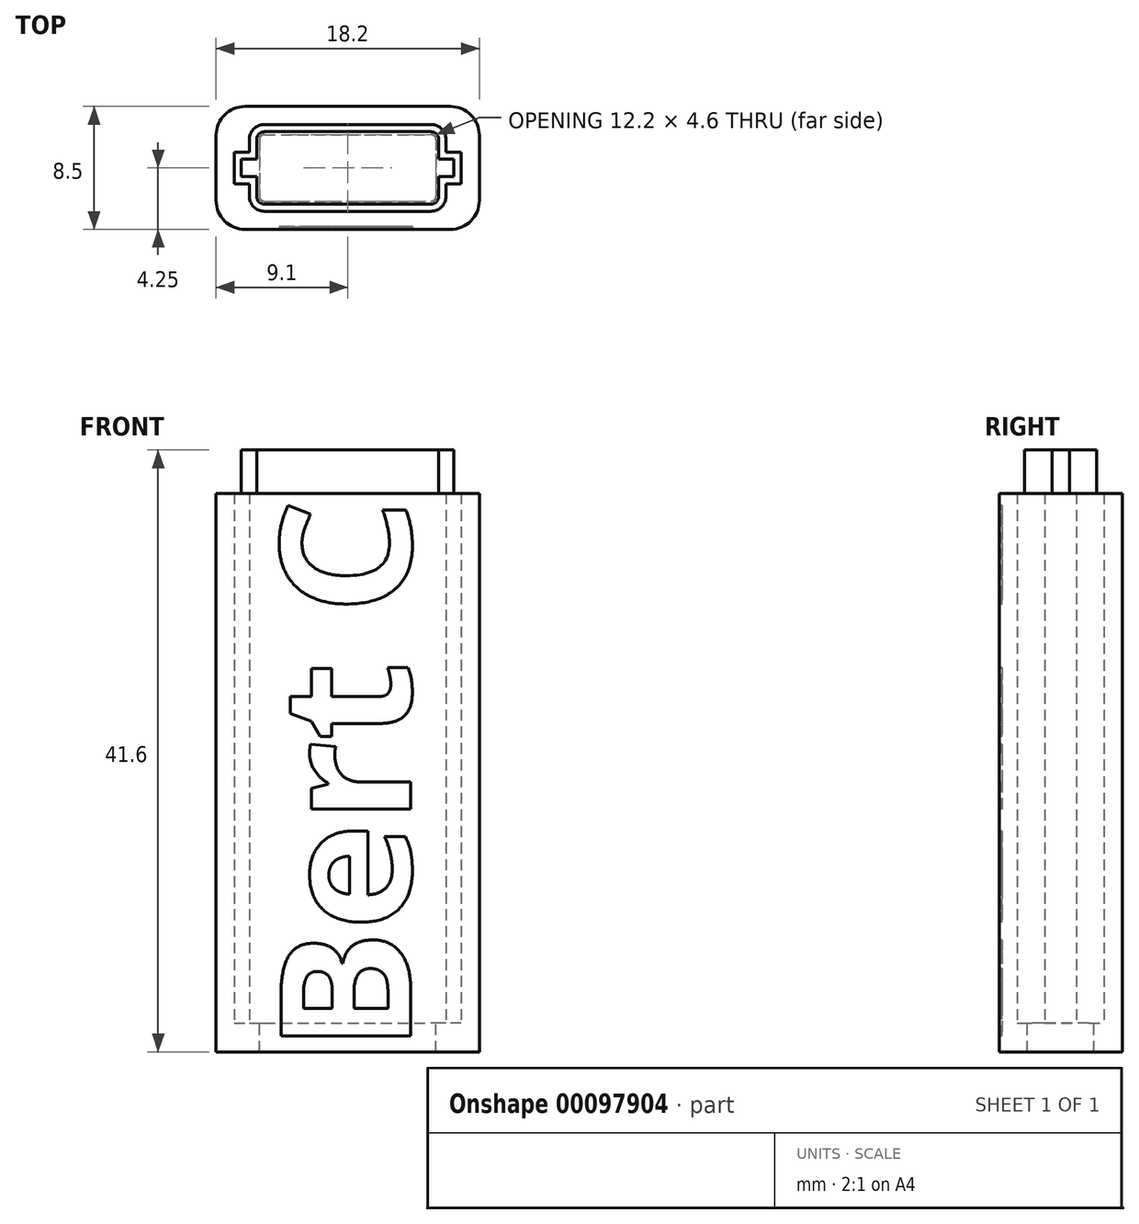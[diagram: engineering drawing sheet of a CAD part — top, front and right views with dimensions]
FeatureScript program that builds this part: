
annotation { "Feature Type Name" : "Feature", "Feature Type Description" : "" }
export const myFeature = defineFeature(function(context is Context, id is Id, definition is map)
    precondition{}
    {
        {
            var Q0;
            Q0=qCreatedBy(makeId("Top.planeOp"),FACE);
            var sketch = newSketch(context, id + "F0", { "sketchPlane" : qUnion([Q0])});
            skLineSegment(sketch, "E0.bottom", {"start": v(-5.75, 2.1) * mm, "end": v(5.75, 2.1) * mm});
            skLineSegment(sketch, "E0.top", {"start": v(-5.75, -2.3) * mm, "end": v(5.75, -2.3) * mm});
            skLineSegment(sketch, "E0.left", {"start": v(-6, 1.85) * mm, "end": v(-6, 0.2) * mm});
            skLineSegment(sketch, "E0.right", {"start": v(6, 1.85) * mm, "end": v(6, 0.2) * mm});
            skPoint(sketch, "E1.visualSharp", {"position": v(-6, 2.1) * mm});
            skArc(sketch, "E1.filletArc", {"start": v(-5.75, 2.1) * mm, "mid": v(-5.93, 2.03) * mm, "end": v(-6, 1.85) * mm});
            skPoint(sketch, "E2.visualSharp", {"position": v(-6, -2.3) * mm});
            skArc(sketch, "E2.filletArc", {"start": v(-6, -2.05) * mm, "mid": v(-5.93, -2.23) * mm, "end": v(-5.75, -2.3) * mm});
            skPoint(sketch, "E3.visualSharp", {"position": v(6, 2.1) * mm});
            skArc(sketch, "E3.filletArc", {"start": v(6, 1.85) * mm, "mid": v(5.93, 2.03) * mm, "end": v(5.75, 2.1) * mm});
            skPoint(sketch, "E4.visualSharp", {"position": v(6, -2.3) * mm});
            skArc(sketch, "E4.filletArc", {"start": v(5.75, -2.3) * mm, "mid": v(5.93, -2.23) * mm, "end": v(6, -2.05) * mm});
            skPoint(sketch, "E5", {"position": v(-6, -0.1) * mm});
            skPoint(sketch, "E6", {"position": v(6, -0.1) * mm});
            skLineSegment(sketch, "E7", {"start": v(-6, -0.1) * mm, "end": v(-7.05, -0.1) * mm});
            skLineSegment(sketch, "E8", {"start": v(6, -0.1) * mm, "end": v(7.05, -0.1) * mm});
            skLineSegment(sketch, "E9", {"start": v(-7.05, -0.1) * mm, "end": v(-7.05, 0.2) * mm});
            skLineSegment(sketch, "E10", {"start": v(-7.05, 0.2) * mm, "end": v(-6, 0.2) * mm});
            skLineSegment(sketch, "E11", {"start": v(-7.05, -0.1) * mm, "end": v(-7.05, -0.4) * mm});
            skLineSegment(sketch, "E12", {"start": v(-7.05, -0.4) * mm, "end": v(-6, -0.4) * mm});
            skLineSegment(sketch, "E13", {"start": v(7.05, -0.1) * mm, "end": v(7.05, -0.4) * mm});
            skLineSegment(sketch, "E14", {"start": v(7.05, -0.4) * mm, "end": v(6, -0.4) * mm});
            skLineSegment(sketch, "E15", {"start": v(7.05, -0.1) * mm, "end": v(7.05, 0.2) * mm});
            skLineSegment(sketch, "E16", {"start": v(7.05, 0.2) * mm, "end": v(6, 0.2) * mm});
            skPoint(sketch, "E17.end.orphan", {"position": v(-7.05, 2.1) * mm});
            skPoint(sketch, "E18.orphan", {"position": v(-7.05, -2.3) * mm});
            skPoint(sketch, "E19.end.orphan", {"position": v(7.05, 2.1) * mm});
            skPoint(sketch, "E20.orphan", {"position": v(7.05, -2.3) * mm});
            skLineSegment(sketch, "E21", {"start": v(-6, 0.2) * mm, "end": v(-6, -0.4) * mm});
            skLineSegment(sketch, "E22", {"start": v(-6, -0.4) * mm, "end": v(-6, -2.05) * mm});
            skLineSegment(sketch, "E23", {"start": v(6, -0.4) * mm, "end": v(6, -2.05) * mm});
            skLineSegment(sketch, "E24", {"start": v(6, 0.2) * mm, "end": v(6, -0.4) * mm});
            skArc(sketch, "E25.0", {"start": v(-5.75, 2.9) * mm, "mid": v(-6.5, 2.6) * mm, "end": v(-6.8, 1.85) * mm});
            skLineSegment(sketch, "E25.1", {"start": v(-5.75, 2.9) * mm, "end": v(5.75, 2.9) * mm});
            skArc(sketch, "E25.2", {"start": v(6.8, 1.85) * mm, "mid": v(6.5, 2.6) * mm, "end": v(5.75, 2.9) * mm});
            skLineSegment(sketch, "E25.3", {"start": v(6.8, 1.85) * mm, "end": v(6.8, 1) * mm});
            skLineSegment(sketch, "E25.4", {"start": v(7.85, 1) * mm, "end": v(6.8, 1) * mm});
            skLineSegment(sketch, "E25.5", {"start": v(-6.8, 1.85) * mm, "end": v(-6.8, 1) * mm});
            skLineSegment(sketch, "E25.6", {"start": v(7.85, 0) * mm, "end": v(7.85, 1) * mm});
            skLineSegment(sketch, "E25.7", {"start": v(7.85, 0) * mm, "end": v(7.85, -1.2) * mm});
            skLineSegment(sketch, "E25.8", {"start": v(-7.85, -1.2) * mm, "end": v(-6.8, -1.2) * mm});
            skLineSegment(sketch, "E25.9", {"start": v(-7.85, 0) * mm, "end": v(-7.85, -1.2) * mm});
            skLineSegment(sketch, "E25.10", {"start": v(-7.85, 0) * mm, "end": v(-7.85, 1) * mm});
            skLineSegment(sketch, "E25.11", {"start": v(-7.85, 1) * mm, "end": v(-6.8, 1) * mm});
            skLineSegment(sketch, "E25.12", {"start": v(-6.8, -1.2) * mm, "end": v(-6.8, -2.05) * mm});
            skArc(sketch, "E25.13", {"start": v(-6.8, -2.05) * mm, "mid": v(-6.5, -2.8) * mm, "end": v(-5.75, -3.1) * mm});
            skLineSegment(sketch, "E25.14", {"start": v(-5.75, -3.1) * mm, "end": v(5.75, -3.1) * mm});
            skArc(sketch, "E25.15", {"start": v(5.75, -3.1) * mm, "mid": v(6.5, -2.8) * mm, "end": v(6.8, -2.05) * mm});
            skLineSegment(sketch, "E25.16", {"start": v(6.8, -1.2) * mm, "end": v(6.8, -2.05) * mm});
            skLineSegment(sketch, "E25.17", {"start": v(7.85, -1.2) * mm, "end": v(6.8, -1.2) * mm});
            skLineSegment(sketch, "E26.0", {"start": v(-7.1, -4.35) * mm, "end": v(7.1, -4.35) * mm});
            skLineSegment(sketch, "E27.0", {"start": v(-7.1, 4.15) * mm, "end": v(7.1, 4.15) * mm});
            skLineSegment(sketch, "E28.0", {"start": v(-9.1, -2.35) * mm, "end": v(-9.1, 2.15) * mm});
            skLineSegment(sketch, "E29.0", {"start": v(9.1, -2.35) * mm, "end": v(9.1, 2.15) * mm});
            skPoint(sketch, "E30.visualSharp", {"position": v(-9.1, 4.15) * mm});
            skArc(sketch, "E30.filletArc", {"start": v(-7.1, 4.15) * mm, "mid": v(-8.51, 3.56) * mm, "end": v(-9.1, 2.15) * mm});
            skPoint(sketch, "E31.visualSharp", {"position": v(-9.1, -4.35) * mm});
            skArc(sketch, "E31.filletArc", {"start": v(-9.1, -2.35) * mm, "mid": v(-8.51, -3.76) * mm, "end": v(-7.1, -4.35) * mm});
            skPoint(sketch, "E32.visualSharp", {"position": v(9.1, -4.35) * mm});
            skArc(sketch, "E32.filletArc", {"start": v(7.1, -4.35) * mm, "mid": v(8.51, -3.76) * mm, "end": v(9.1, -2.35) * mm});
            skPoint(sketch, "E33.visualSharp", {"position": v(9.1, 4.15) * mm});
            skArc(sketch, "E33.filletArc", {"start": v(9.1, 2.15) * mm, "mid": v(8.51, 3.56) * mm, "end": v(7.1, 4.15) * mm});
            skLineSegment(sketch, "E34", {"start": v(-6.8, 1) * mm, "end": v(-6.8, -1.2) * mm});
            skLineSegment(sketch, "E35", {"start": v(6.8, 1) * mm, "end": v(6.8, -1.2) * mm});
            skArc(sketch, "E36.0", {"start": v(-6.1, -2.05) * mm, "mid": v(-6, -2.3) * mm, "end": v(-5.75, -2.4) * mm});
            skLineSegment(sketch, "E36.1", {"start": v(6.1, 1.85) * mm, "end": v(6.1, 0.4) * mm});
            skLineSegment(sketch, "E36.2", {"start": v(6.1, 0.4) * mm, "end": v(6.1, -0.4) * mm});
            skLineSegment(sketch, "E36.3", {"start": v(6.1, -0.4) * mm, "end": v(6.1, -2.05) * mm});
            skArc(sketch, "E36.4", {"start": v(5.75, -2.4) * mm, "mid": v(6, -2.3) * mm, "end": v(6.1, -2.05) * mm});
            skArc(sketch, "E36.5", {"start": v(6.1, 1.85) * mm, "mid": v(6, 2.1) * mm, "end": v(5.75, 2.2) * mm});
            skLineSegment(sketch, "E36.6", {"start": v(-5.75, -2.4) * mm, "end": v(5.75, -2.4) * mm});
            skLineSegment(sketch, "E36.7", {"start": v(-5.75, 2.2) * mm, "end": v(5.75, 2.2) * mm});
            skArc(sketch, "E36.8", {"start": v(-5.75, 2.2) * mm, "mid": v(-6, 2.1) * mm, "end": v(-6.1, 1.85) * mm});
            skLineSegment(sketch, "E36.9", {"start": v(-6.1, 1.85) * mm, "end": v(-6.1, 0.4) * mm});
            skLineSegment(sketch, "E36.10", {"start": v(-6.1, 0.4) * mm, "end": v(-6.1, -0.4) * mm});
            skLineSegment(sketch, "E36.11", {"start": v(-6.1, -0.4) * mm, "end": v(-6.1, -2.05) * mm});
            skSolve(sketch);
        }
        {
            var Q0;
            Q0=makeQuery(id+"F0.imprint","IMPRINT",FACE,{"disambiguationData":[TD([[makeQuery(id+"F0.imprint","IMPRINT",EDGE,{"derivedFrom":sQuery(id+"F0.wireOp",EDGE,"E25.0")}),-1.0]])]});
            extrude(context, id + "F1", {"entities" : qUnion([Q0]), "depth" : 36.6 * mm});
        }
        {
            var Q0;
            {var subQ4=sQuery(id+"F0.wireOp",EDGE,"E9");Q0=makeQuery(id+"F0.imprint","IMPRINT",FACE,{"disambiguationData":[TD([[makeQuery(id+"F0.imprint","IMPRINT",EDGE,{"derivedFrom":subQ4}),1.0]])]});}
            var Q1;
            {var subQ0=sQuery(id+"F0.wireOp",EDGE,"E9");Q1=makeQuery(id+"F0.imprint","IMPRINT",FACE,{"disambiguationData":[TD([[makeQuery(id+"F0.imprint","IMPRINT",EDGE,{"derivedFrom":subQ0}),-1.0]])]});}
            var Q2;
            {var subQ0=sQuery(id+"F0.wireOp",EDGE,"E11");Q2=makeQuery(id+"F0.imprint","IMPRINT",FACE,{"disambiguationData":[TD([[makeQuery(id+"F0.imprint","IMPRINT",EDGE,{"derivedFrom":subQ0}),1.0]])]});}
            var Q3;
            {var subQ0=sQuery(id+"F0.wireOp",EDGE,"E15");Q3=makeQuery(id+"F0.imprint","IMPRINT",FACE,{"disambiguationData":[TD([[makeQuery(id+"F0.imprint","IMPRINT",EDGE,{"derivedFrom":subQ0}),1.0]])]});}
            var Q4;
            {var subQ0=sQuery(id+"F0.wireOp",EDGE,"E13");Q4=makeQuery(id+"F0.imprint","IMPRINT",FACE,{"disambiguationData":[TD([[makeQuery(id+"F0.imprint","IMPRINT",EDGE,{"derivedFrom":subQ0}),-1.0]])]});}
            var Q5;
            {var subQ7=sQuery(id+"F0.wireOp",EDGE,"E13");Q5=makeQuery(id+"F0.imprint","IMPRINT",FACE,{"disambiguationData":[TD([[makeQuery(id+"F0.imprint","IMPRINT",EDGE,{"derivedFrom":subQ7}),1.0]])]});}
            var Q6;
            Q6=makeQuery(id+"F0.imprint","IMPRINT",FACE,{"disambiguationData":[TD([[makeQuery(id+"F0.imprint","IMPRINT",EDGE,{"derivedFrom":sQuery(id+"F0.wireOp",EDGE,"E25.0")}),-1.0]])]});
            var Q7;
            {var subQ1=sQuery(id+"F0.wireOp",EDGE,"E25.12");Q7=makeQuery(id+"F0.imprint","IMPRINT",FACE,{"disambiguationData":[TD([[makeQuery(id+"F0.imprint","IMPRINT",EDGE,{"derivedFrom":subQ1}),1.0]])]});}
            var Q8;
            {var subQ0=sQuery(id+"F0.wireOp",EDGE,"E36.10");var subQ1=sQuery(id+"F0.wireOp",EDGE,"E7");var subQ2=makeQuery(id+"F0.imprint","INTERSECT",VERTEX,{"derivedFrom":[subQ1,subQ0]});Q8=makeQuery(id+"F0.imprint","IMPRINT",FACE,{"disambiguationData":[TD([[makeQuery(id+"F0.imprint","IMPRINT",EDGE,{"disambiguationData":[TD([[subQ2,-1.0]])],"derivedFrom":subQ1}),1.0]])]});}
            var Q9;
            {var subQ0=sQuery(id+"F0.wireOp",EDGE,"E36.10");var subQ1=sQuery(id+"F0.wireOp",EDGE,"E7");var subQ2=makeQuery(id+"F0.imprint","INTERSECT",VERTEX,{"derivedFrom":[subQ1,subQ0]});Q9=makeQuery(id+"F0.imprint","IMPRINT",FACE,{"disambiguationData":[TD([[makeQuery(id+"F0.imprint","IMPRINT",EDGE,{"disambiguationData":[TD([[subQ2,-1.0]])],"derivedFrom":subQ1}),-1.0]])]});}
            var Q10;
            Q10=makeQuery(id+"F0.imprint","IMPRINT",FACE,{"disambiguationData":[TD([[makeQuery(id+"F0.imprint","IMPRINT",EDGE,{"derivedFrom":sQuery(id+"F0.wireOp",EDGE,"E25.0")}),1.0]])]});
            var Q11;
            {var subQ0=sQuery(id+"F0.wireOp",EDGE,"E36.2");var subQ1=sQuery(id+"F0.wireOp",EDGE,"E8");var subQ2=makeQuery(id+"F0.imprint","INTERSECT",VERTEX,{"derivedFrom":[subQ1,subQ0]});Q11=makeQuery(id+"F0.imprint","IMPRINT",FACE,{"disambiguationData":[TD([[makeQuery(id+"F0.imprint","IMPRINT",EDGE,{"disambiguationData":[TD([[subQ2,-1.0]])],"derivedFrom":subQ1}),1.0]])]});}
            var Q12;
            {var subQ0=sQuery(id+"F0.wireOp",EDGE,"E36.2");var subQ1=sQuery(id+"F0.wireOp",EDGE,"E8");var subQ2=makeQuery(id+"F0.imprint","INTERSECT",VERTEX,{"derivedFrom":[subQ1,subQ0]});Q12=makeQuery(id+"F0.imprint","IMPRINT",FACE,{"disambiguationData":[TD([[makeQuery(id+"F0.imprint","IMPRINT",EDGE,{"disambiguationData":[TD([[subQ2,-1.0]])],"derivedFrom":subQ1}),-1.0]])]});}
            extrude(context, id + "F2", {"entities" : qUnion([Q0, Q1, Q2, Q3, Q4, Q5, Q6, Q7, Q8, Q9, Q10, Q11, Q12]), "operationType" : NewBodyOperationType.ADD, "oppositeDirection" : true, "depth" : 2 * mm});
        }
        {
            var Q0;
            {var subQ0=sQuery(id+"F0.wireOp",EDGE,"E26.0");Q0=makeQuery(id+"F2.boolean.opBoolean","MERGE",FACE,{"derivedFrom":[makeQuery(id+"F1.opExtrude","SWEPT_FACE",FACE,{"disambiguationData":[OSD([subQ0])]}),makeQuery(id+"F2.opExtrude","SWEPT_FACE",FACE,{"disambiguationData":[OSD([subQ0])]})]});}
            var sketch = newSketch(context, id + "F3", { "sketchPlane" : qUnion([Q0])});
            skLineSegment(sketch, "E37.1", {"start": v(-7.1, 36.6) * mm, "end": v(7.1, 36.6) * mm});
            skLineSegment(sketch, "E37.2", {"start": v(-7.1, 36.6) * mm, "end": v(-7.1, -2) * mm});
            skLineSegment(sketch, "E37.3", {"start": v(7.1, 36.6) * mm, "end": v(7.1, -2) * mm});
            skLineSegment(sketch, "E37.4", {"start": v(-7.1, -2) * mm, "end": v(7.1, -2) * mm});
            skText(sketch, "E38", { "text": "Bert C", "fontName": "OpenSans-Bold.ttf"});
            const initialGuessF3  = {"E38": [0.00435, -0.00204, 0, 1, 0.00904]};
            skSetInitialGuess(sketch, initialGuessF3);
            skSolve(sketch);
        }
        {
            var Q0;
            Q0=makeQuery(id+"F3.imprint","IMPRINT",FACE,{"disambiguationData":[TD([[makeQuery(id+"F3.imprint","IMPRINT",EDGE,{"derivedFrom":sQuery(id+"F3.wireOp",EDGE,"E38.sketch_text.stroke-76")}),-1.0]])]});
            var Q1;
            Q1=makeQuery(id+"F3.imprint","IMPRINT",FACE,{"disambiguationData":[TD([[makeQuery(id+"F3.imprint","IMPRINT",EDGE,{"derivedFrom":sQuery(id+"F3.wireOp",EDGE,"E38.sketch_text.stroke-58")}),-1.0]])]});
            var Q2;
            Q2=makeQuery(id+"F3.imprint","IMPRINT",FACE,{"disambiguationData":[TD([[makeQuery(id+"F3.imprint","IMPRINT",EDGE,{"derivedFrom":sQuery(id+"F3.wireOp",EDGE,"E38.sketch_text.stroke-45")}),-1.0]])]});
            var Q3;
            Q3=makeQuery(id+"F3.imprint","IMPRINT",FACE,{"disambiguationData":[TD([[makeQuery(id+"F3.imprint","IMPRINT",EDGE,{"derivedFrom":sQuery(id+"F3.wireOp",EDGE,"E38.sketch_text.stroke-25")}),-1.0]])]});
            var Q4;
            Q4=makeQuery(id+"F3.imprint","IMPRINT",FACE,{"disambiguationData":[TD([[makeQuery(id+"F3.imprint","IMPRINT",EDGE,{"derivedFrom":sQuery(id+"F3.wireOp",EDGE,"E38.sketch_text.stroke-0")}),-1.0]])]});
            extrude(context, id + "F4", {"entities" : qUnion([Q0, Q1, Q2, Q3, Q4]), "operationType" : NewBodyOperationType.REMOVE, "oppositeDirection" : true, "depth" : .2 * mm});
        }
        {
            var Q0;
            Q0=makeQuery(id+"F1.opExtrude","CAP_FACE",FACE,{"disambiguationData":[OSD([sQuery(id+"F0.wireOp",EDGE,"E25.0"),sQuery(id+"F0.wireOp",EDGE,"E25.1"),sQuery(id+"F0.wireOp",EDGE,"E25.2"),sQuery(id+"F0.wireOp",EDGE,"E25.3"),sQuery(id+"F0.wireOp",EDGE,"E25.4"),sQuery(id+"F0.wireOp",EDGE,"E25.5"),sQuery(id+"F0.wireOp",EDGE,"E25.6"),sQuery(id+"F0.wireOp",EDGE,"E25.7"),sQuery(id+"F0.wireOp",EDGE,"E25.8"),sQuery(id+"F0.wireOp",EDGE,"E25.9"),sQuery(id+"F0.wireOp",EDGE,"E25.10"),sQuery(id+"F0.wireOp",EDGE,"E25.11"),sQuery(id+"F0.wireOp",EDGE,"E25.12"),sQuery(id+"F0.wireOp",EDGE,"E25.13"),sQuery(id+"F0.wireOp",EDGE,"E25.14"),sQuery(id+"F0.wireOp",EDGE,"E25.15"),sQuery(id+"F0.wireOp",EDGE,"E25.16"),sQuery(id+"F0.wireOp",EDGE,"E25.17"),sQuery(id+"F0.wireOp",EDGE,"E26.0"),sQuery(id+"F0.wireOp",EDGE,"E27.0"),sQuery(id+"F0.wireOp",EDGE,"E28.0"),sQuery(id+"F0.wireOp",EDGE,"E29.0"),sQuery(id+"F0.wireOp",EDGE,"E30.filletArc"),sQuery(id+"F0.wireOp",EDGE,"E31.filletArc"),sQuery(id+"F0.wireOp",EDGE,"E32.filletArc"),sQuery(id+"F0.wireOp",EDGE,"E33.filletArc")])],"isStart":false});
            var sketch = newSketch(context, id + "F5", { "sketchPlane" : qUnion([Q0])});
            skLineSegment(sketch, "E39.0", {"start": v(7.35, -0.7) * mm, "end": v(6.3, -0.7) * mm});
            skLineSegment(sketch, "E39.1", {"start": v(7.35, -0.7) * mm, "end": v(7.35, 0.5) * mm});
            skLineSegment(sketch, "E39.2", {"start": v(7.35, 0.5) * mm, "end": v(6.3, 0.5) * mm});
            skLineSegment(sketch, "E39.3", {"start": v(6.3, 1.85) * mm, "end": v(6.3, 0.5) * mm});
            skArc(sketch, "E39.4", {"start": v(6.3, 1.85) * mm, "mid": v(6.14, 2.24) * mm, "end": v(5.75, 2.4) * mm});
            skLineSegment(sketch, "E39.5", {"start": v(-6.3, -0.7) * mm, "end": v(-6.3, -2.05) * mm});
            skArc(sketch, "E39.6", {"start": v(-6.3, -2.05) * mm, "mid": v(-6.14, -2.44) * mm, "end": v(-5.75, -2.6) * mm});
            skLineSegment(sketch, "E39.7", {"start": v(-5.75, -2.6) * mm, "end": v(5.75, -2.6) * mm});
            skArc(sketch, "E39.8", {"start": v(5.75, -2.6) * mm, "mid": v(6.14, -2.44) * mm, "end": v(6.3, -2.05) * mm});
            skLineSegment(sketch, "E39.9", {"start": v(-7.35, -0.7) * mm, "end": v(-6.3, -0.7) * mm});
            skLineSegment(sketch, "E39.10", {"start": v(-7.35, 0.5) * mm, "end": v(-7.35, -0.7) * mm});
            skLineSegment(sketch, "E39.11", {"start": v(-7.35, 0.5) * mm, "end": v(-6.3, 0.5) * mm});
            skLineSegment(sketch, "E39.12", {"start": v(-6.3, 1.85) * mm, "end": v(-6.3, 0.5) * mm});
            skArc(sketch, "E39.13", {"start": v(-5.75, 2.4) * mm, "mid": v(-6.14, 2.24) * mm, "end": v(-6.3, 1.85) * mm});
            skLineSegment(sketch, "E39.14", {"start": v(6.3, -0.7) * mm, "end": v(6.3, -2.05) * mm});
            skLineSegment(sketch, "E39.15", {"start": v(-5.75, 2.4) * mm, "end": v(5.75, 2.4) * mm});
            skSolve(sketch);
        }
        {
            var Q0;
            Q0 = qSketchRegion(id + "F5", true);
            extrude(context, id + "F6", {"entities" : qUnion([Q0]), "depth" : 3 * mm});
        }
    });
